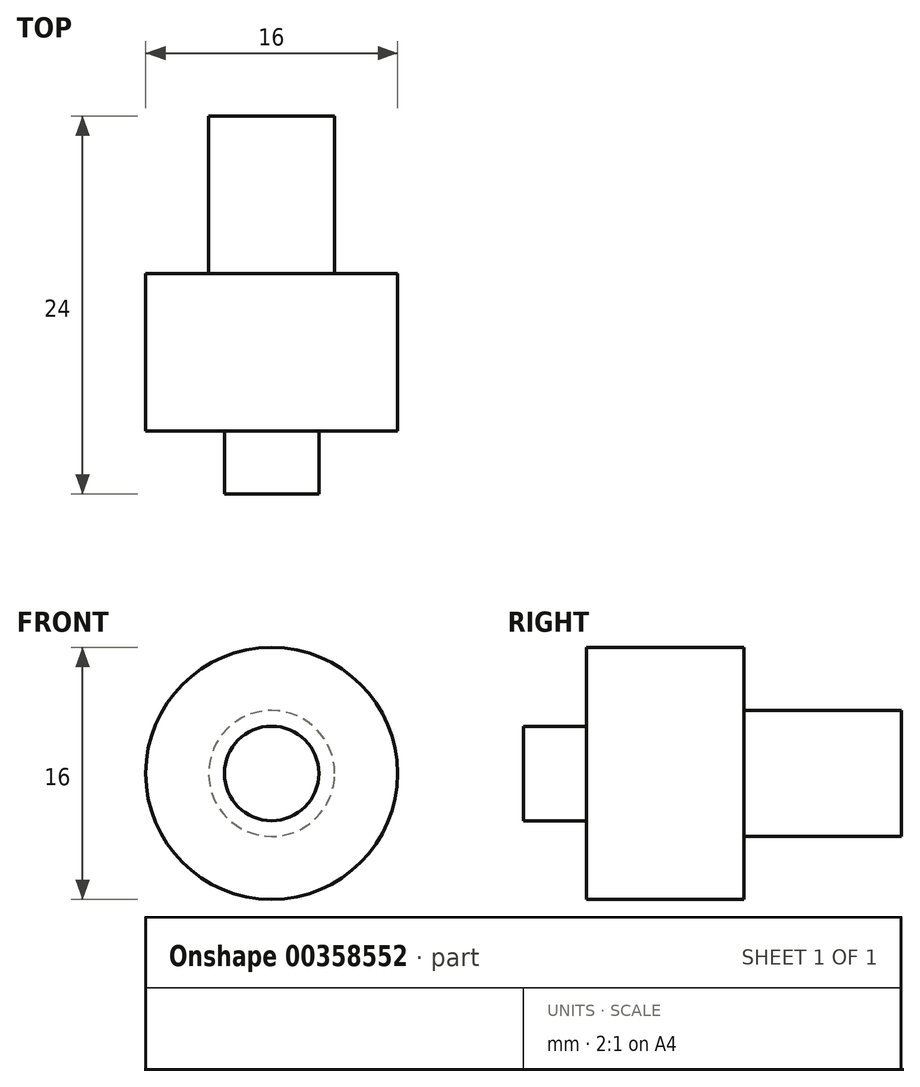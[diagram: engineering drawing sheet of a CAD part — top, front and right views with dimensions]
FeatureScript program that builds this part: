
annotation { "Feature Type Name" : "Feature", "Feature Type Description" : "" }
export const myFeature = defineFeature(function(context is Context, id is Id, definition is map)
    precondition{}
    {
        {
            var Q0;
            Q0=qCreatedBy(makeId("Front.planeOp"),FACE);
            var sketch = newSketch(context, id + "F0", { "sketchPlane" : qUnion([Q0])});
            skCircle(sketch, "E0", {"center": v(0, 0) * mm, "radius": 8 * mm});
            skSolve(sketch);
        }
        {
            var Q0;
            Q0 = qSketchRegion(id + "F0", true);
            extrude(context, id + "F1", {"entities" : qUnion([Q0]), "oppositeDirection" : true, "depth" : 24 * mm});
        }
        {
            var Q0;
            Q0=makeQuery(id+"F1.opExtrude","CAP_FACE",FACE,{"disambiguationData":[OSD([sQuery(id+"F0.wireOp",EDGE,"E0")])],"isStart":true});
            var sketch = newSketch(context, id + "F2", { "sketchPlane" : qUnion([Q0])});
            skCircle(sketch, "E1", {"center": v(0, 0) * mm, "radius": 12.16 * mm});
            skCircle(sketch, "E2", {"center": v(0, 0) * mm, "radius": 3 * mm});
            skSolve(sketch);
        }
        {
            var Q0;
            Q0 = qSketchRegion(id + "F2", true);
            extrude(context, id + "F3", {"entities" : qUnion([Q0]), "operationType" : NewBodyOperationType.REMOVE, "oppositeDirection" : true, "depth" : 4 * mm});
        }
        {
            var Q0;
            Q0=makeQuery(id+"F1.opExtrude","CAP_FACE",FACE,{"disambiguationData":[OSD([sQuery(id+"F0.wireOp",EDGE,"E0")])],"isStart":false});
            var sketch = newSketch(context, id + "F4", { "sketchPlane" : qUnion([Q0])});
            skCircle(sketch, "E3", {"center": v(0, 0) * mm, "radius": 10.91 * mm});
            skCircle(sketch, "E4", {"center": v(0, 0) * mm, "radius": 4 * mm});
            skSolve(sketch);
        }
        {
            var Q0;
            Q0 = qSketchRegion(id + "F4", true);
            extrude(context, id + "F5", {"entities" : qUnion([Q0]), "operationType" : NewBodyOperationType.REMOVE, "oppositeDirection" : true, "depth" : 10 * mm});
        }
    });
